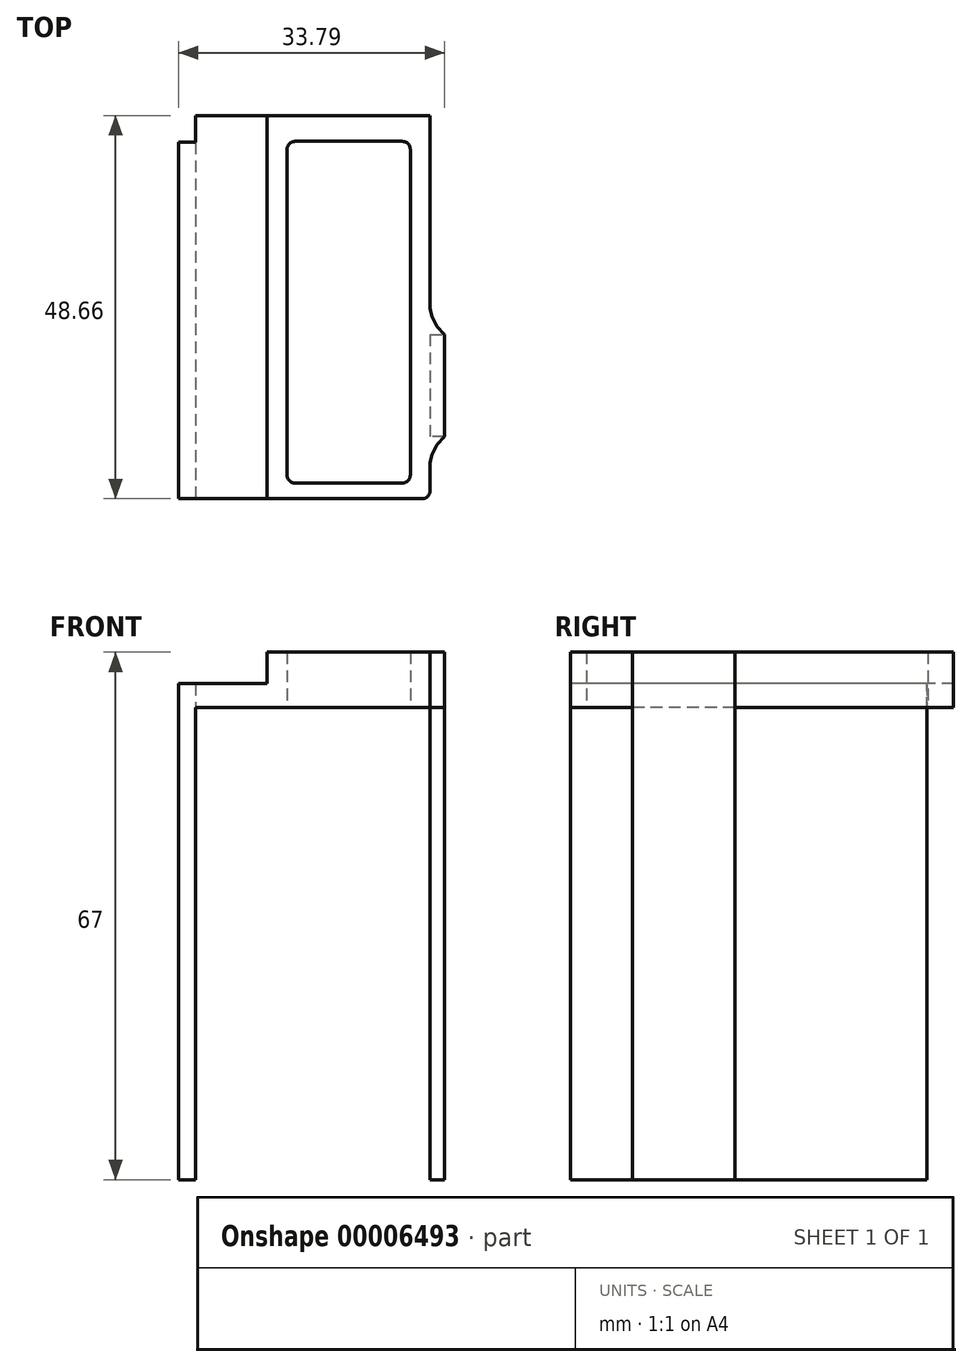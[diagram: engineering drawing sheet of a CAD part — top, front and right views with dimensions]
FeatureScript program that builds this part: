
annotation { "Feature Type Name" : "Feature", "Feature Type Description" : "" }
export const myFeature = defineFeature(function(context is Context, id is Id, definition is map)
    precondition{}
    {
        {
            var Q0;
            Q0=qCreatedBy(makeId("Top.planeOp"),FACE);
            var sketch = newSketch(context, id + "F0", { "sketchPlane" : qUnion([Q0])});
            skLineSegment(sketch, "E0.bottom", {"start": v(-57.76, 17.92) * mm, "end": v(-44.1, 17.92) * mm});
            skLineSegment(sketch, "E0.top", {"start": v(-57.76, -25.48) * mm, "end": v(-44.1, -25.48) * mm});
            skLineSegment(sketch, "E0.left", {"start": v(-58.76, 16.92) * mm, "end": v(-58.76, -24.48) * mm});
            skLineSegment(sketch, "E0.right", {"start": v(-43.1, 16.92) * mm, "end": v(-43.1, -24.48) * mm});
            skLineSegment(sketch, "E1.bottom", {"start": v(-69.36, 36.96) * mm, "end": v(-41.6, 36.96) * mm});
            skLineSegment(sketch, "E1.top", {"start": v(-69.36, -27.48) * mm, "end": v(-41.6, -27.48) * mm});
            skLineSegment(sketch, "E1.left", {"start": v(-70.36, 35.96) * mm, "end": v(-70.36, -26.48) * mm});
            skLineSegment(sketch, "E1.right", {"start": v(-40.6, 35.96) * mm, "end": v(-40.6, -26.48) * mm});
            skPoint(sketch, "E2.visualSharp", {"position": v(-70.36, 36.96) * mm});
            skArc(sketch, "E2.filletArc", {"start": v(-69.36, 36.96) * mm, "mid": v(-70.06, 36.67) * mm, "end": v(-70.36, 35.96) * mm});
            skPoint(sketch, "E3.visualSharp", {"position": v(-40.6, 36.96) * mm});
            skArc(sketch, "E3.filletArc", {"start": v(-40.6, 35.96) * mm, "mid": v(-40.89, 36.67) * mm, "end": v(-41.6, 36.96) * mm});
            skPoint(sketch, "E4.visualSharp", {"position": v(-70.36, -27.48) * mm});
            skArc(sketch, "E4.filletArc", {"start": v(-70.36, -26.48) * mm, "mid": v(-70.06, -27.19) * mm, "end": v(-69.36, -27.48) * mm});
            skPoint(sketch, "E5.visualSharp", {"position": v(-40.6, -27.48) * mm});
            skArc(sketch, "E5.filletArc", {"start": v(-41.6, -27.48) * mm, "mid": v(-40.89, -27.19) * mm, "end": v(-40.6, -26.48) * mm});
            skPoint(sketch, "E6.visualSharp", {"position": v(-58.76, 17.92) * mm});
            skArc(sketch, "E6.filletArc", {"start": v(-57.76, 17.92) * mm, "mid": v(-58.46, 17.62) * mm, "end": v(-58.76, 16.92) * mm});
            skPoint(sketch, "E7.visualSharp", {"position": v(-43.1, 17.92) * mm});
            skArc(sketch, "E7.filletArc", {"start": v(-43.1, 16.92) * mm, "mid": v(-43.39, 17.62) * mm, "end": v(-44.1, 17.92) * mm});
            skPoint(sketch, "E8.visualSharp", {"position": v(-43.1, -25.48) * mm});
            skArc(sketch, "E8.filletArc", {"start": v(-44.1, -25.48) * mm, "mid": v(-43.39, -25.19) * mm, "end": v(-43.1, -24.48) * mm});
            skPoint(sketch, "E9.visualSharp", {"position": v(-58.76, -25.48) * mm});
            skArc(sketch, "E9.filletArc", {"start": v(-58.76, -24.48) * mm, "mid": v(-58.46, -25.19) * mm, "end": v(-57.76, -25.48) * mm});
            skLineSegment(sketch, "E10", {"start": v(-40.6, -6.6) * mm, "end": v(-38.74, -6.6) * mm});
            skLineSegment(sketch, "E11", {"start": v(-38.74, -6.6) * mm, "end": v(-38.74, -19.6) * mm});
            skLineSegment(sketch, "E12", {"start": v(-38.74, -19.6) * mm, "end": v(-40.6, -19.6) * mm});
            skLineSegment(sketch, "E13", {"start": v(-70.36, 17.8) * mm, "end": v(-72.53, 17.8) * mm});
            skLineSegment(sketch, "E14", {"start": v(-72.53, 17.8) * mm, "end": v(-72.53, -20.69) * mm});
            skLineSegment(sketch, "E15", {"start": v(-72.53, -20.69) * mm, "end": v(-70.36, -20.69) * mm});
            skLineSegment(sketch, "E16", {"start": v(-40.6, 21.18) * mm, "end": v(-61.32, 21.18) * mm});
            skLineSegment(sketch, "E17", {"start": v(-61.32, 21.18) * mm, "end": v(-61.32, -27.48) * mm});
            skLineSegment(sketch, "E18", {"start": v(-61.32, 21.18) * mm, "end": v(-70.36, 21.18) * mm});
            skLineSegment(sketch, "E19", {"start": v(-72.53, -20.69) * mm, "end": v(-72.53, -27.48) * mm});
            skLineSegment(sketch, "E20", {"start": v(-72.53, -27.48) * mm, "end": v(-69.36, -27.48) * mm});
            skLineSegment(sketch, "E21", {"start": v(-70.36, -26.48) * mm, "end": v(-70.36, -27.48) * mm});
            skSolve(sketch);
        }
        {
            var Q0;
            Q0=makeQuery(id+"F0.imprint","IMPRINT",FACE,{"disambiguationData":[TD([[makeQuery(id+"F0.imprint","IMPRINT",EDGE,{"derivedFrom":sQuery(id+"F0.wireOp",EDGE,"E0.bottom")}),1.0]])]});
            var Q1;
            {var subQ1=sQuery(id+"F0.wireOp",EDGE,"E10");Q1=makeQuery(id+"F0.imprint","IMPRINT",FACE,{"disambiguationData":[TD([[makeQuery(id+"F0.imprint","IMPRINT",EDGE,{"derivedFrom":subQ1}),-1.0]])]});}
            extrude(context, id + "F1", {"entities" : qUnion([Q0, Q1]), "depth" : 7 * mm});
        }
        {
            var Q0;
            {var subQ1=sQuery(id+"F0.wireOp",EDGE,"E13");Q0=makeQuery(id+"F0.imprint","IMPRINT",FACE,{"disambiguationData":[TD([[makeQuery(id+"F0.imprint","IMPRINT",EDGE,{"derivedFrom":subQ1}),1.0]])]});}
            var Q1;
            {var subQ1=sQuery(id+"F0.wireOp",EDGE,"E10");Q1=makeQuery(id+"F0.imprint","IMPRINT",FACE,{"disambiguationData":[TD([[makeQuery(id+"F0.imprint","IMPRINT",EDGE,{"derivedFrom":subQ1}),-1.0]])]});}
            var Q2;
            {var subQ3=sQuery(id+"F0.wireOp",EDGE,"E15");Q2=makeQuery(id+"F0.imprint","IMPRINT",FACE,{"disambiguationData":[TD([[makeQuery(id+"F0.imprint","IMPRINT",EDGE,{"derivedFrom":subQ3}),-1.0]])]});}
            extrude(context, id + "F2", {"entities" : qUnion([Q0, Q1, Q2]), "operationType" : NewBodyOperationType.ADD, "oppositeDirection" : true, "depth" : 60 * mm});
        }
        {
            var Q0;
            {var subQ2=sQuery(id+"F0.wireOp",EDGE,"E4.filletArc");Q0=makeQuery(id+"F0.imprint","IMPRINT",FACE,{"disambiguationData":[TD([[makeQuery(id+"F0.imprint","IMPRINT",EDGE,{"derivedFrom":subQ2}),1.0]])]});}
            var Q1;
            {var subQ1=sQuery(id+"F0.wireOp",EDGE,"E13");Q1=makeQuery(id+"F0.imprint","IMPRINT",FACE,{"disambiguationData":[TD([[makeQuery(id+"F0.imprint","IMPRINT",EDGE,{"derivedFrom":subQ1}),1.0]])]});}
            var Q2;
            {var subQ3=sQuery(id+"F0.wireOp",EDGE,"E15");Q2=makeQuery(id+"F0.imprint","IMPRINT",FACE,{"disambiguationData":[TD([[makeQuery(id+"F0.imprint","IMPRINT",EDGE,{"derivedFrom":subQ3}),-1.0]])]});}
            var Q3;
            {var subQ2=sQuery(id+"F0.wireOp",EDGE,"E4.filletArc");Q3=makeQuery(id+"F0.imprint","IMPRINT",FACE,{"disambiguationData":[TD([[makeQuery(id+"F0.imprint","IMPRINT",EDGE,{"derivedFrom":subQ2}),-1.0]])]});}
            extrude(context, id + "F3", {"entities" : qUnion([Q0, Q1, Q2, Q3]), "operationType" : NewBodyOperationType.ADD, "depth" : 3 * mm});
        }
        {
            var Q0;
            Q0=makeQuery(id+"F1.opExtrude","SWEPT_EDGE",EDGE,{"disambiguationData":[OSD([sQuery(id+"F0.wireOp",EDGE,"E1.right"),sQuery(id+"F0.wireOp",EDGE,"E12")])]});
            var Q1;
            Q1=makeQuery(id+"F1.opExtrude","SWEPT_EDGE",EDGE,{"disambiguationData":[OSD([sQuery(id+"F0.wireOp",EDGE,"E1.right"),sQuery(id+"F0.wireOp",EDGE,"E10")])]});
            fillet(context, id + "F4", {"entities" : qUnion([Q0, Q1]), "radius" : 5 * mm, "tangentPropagation" : true, "allowEdgeOverflow" : false});
        }
    });
